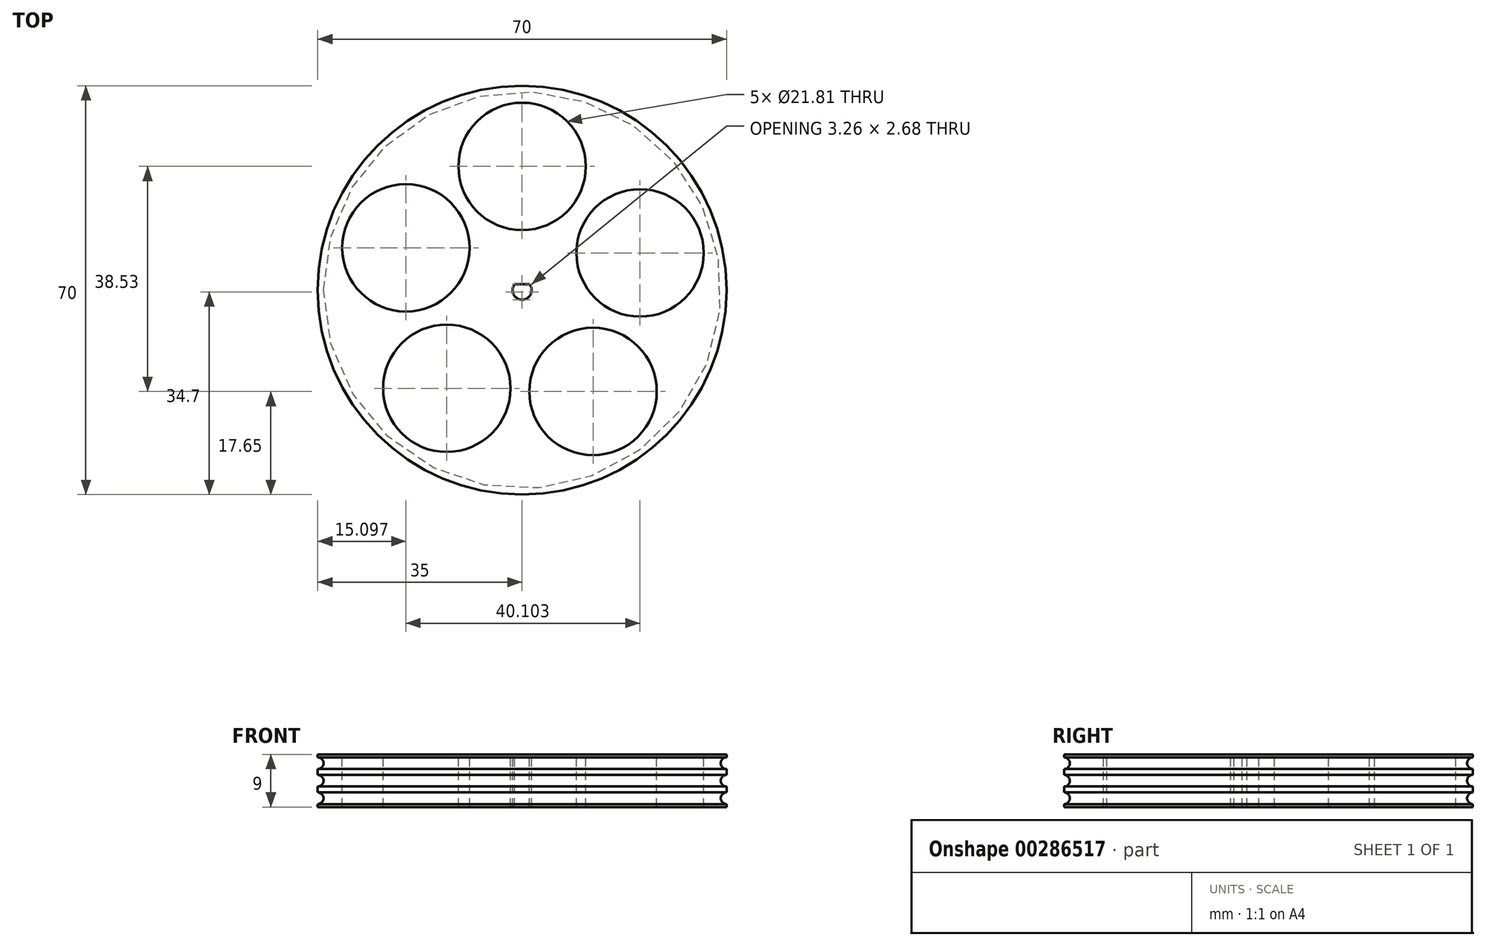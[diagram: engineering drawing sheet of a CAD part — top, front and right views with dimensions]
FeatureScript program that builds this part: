
annotation { "Feature Type Name" : "Feature", "Feature Type Description" : "" }
export const myFeature = defineFeature(function(context is Context, id is Id, definition is map)
    precondition{}
    {
        {
            var Q0;
            Q0=qCreatedBy(makeId("Front.planeOp"),FACE);
            var sketch = newSketch(context, id + "F0", { "sketchPlane" : qUnion([Q0])});
            skLineSegment(sketch, "E0.bottom", {"start": v(0, 0) * mm, "end": v(0, 9) * mm});
            skLineSegment(sketch, "E0.top", {"start": v(-35, 0) * mm, "end": v(-35, 9) * mm});
            skLineSegment(sketch, "E0.left", {"start": v(0, 0) * mm, "end": v(-35, 0) * mm});
            skLineSegment(sketch, "E0.right", {"start": v(0, 9) * mm, "end": v(-35, 9) * mm});
            skCircle(sketch, "E1", {"center": v(-35, 1.5) * mm, "radius": 1 * mm});
            skCircle(sketch, "E2.1.0.0", {"center": v(-35, 4.5) * mm, "radius": 1 * mm});
            skCircle(sketch, "E2.2.0.0", {"center": v(-35, 7.5) * mm, "radius": 1 * mm});
            skLineSegment(sketch, "E2.direction1", {"start": v(-35, 1.5) * mm, "end": v(-35, 4.5) * mm, "construction": true});
            skSolve(sketch);
        }
        {
            var Q0;
            Q0=makeQuery(id+"F0.imprint","IMPRINT",FACE,{"disambiguationData":[TD([[makeQuery(id+"F0.imprint","IMPRINT",EDGE,{"derivedFrom":sQuery(id+"F0.wireOp",EDGE,"E0.bottom")}),1.0]])]});
            var Q1;
            Q1=sQuery(id+"F0.wireOp",EDGE,"E0.bottom");
            revolve(context, id + "F1", {"surfaceOperationType" : NewSurfaceOperationType.NEW, "entities" : qUnion([Q0]), "axis" : qUnion([Q1]), "revolveType" : RevolveType.FULL});
        }
        {
            var Q0;
            Q0=makeQuery(id+"F1.opRevolve","SWEPT_FACE",FACE,{"disambiguationData":[OSD([sQuery(id+"F0.wireOp",EDGE,"E0.right")])]});
            var sketch = newSketch(context, id + "F2", { "sketchPlane" : qUnion([Q0])});
            skLineSegment(sketch, "E3", {"start": v(-1.2, 0.9) * mm, "end": v(1.2, 0.9) * mm, "construction": true});
            skArc(sketch, "E4", {"start": v(-1.2, 0.9) * mm, "mid": v(0, -1.5) * mm, "end": v(1.2, 0.9) * mm, "construction": true});
            skLineSegment(sketch, "E5.0", {"start": v(-1.27, 1.04) * mm, "end": v(1.27, 1.04) * mm});
            skArc(sketch, "E5.1", {"start": v(-1.27, 1.04) * mm, "mid": v(0, -1.64) * mm, "end": v(1.27, 1.04) * mm});
            skSolve(sketch);
        }
        {
            var Q0;
            Q0=qSketchRegion(id+"F2",true);
            extrude(context, id + "F3", {"entities" : qUnion([Q0]), "operationType" : NewBodyOperationType.REMOVE, "endBound" : BoundingType.THROUGH_ALL, "oppositeDirection" : true, "depth" : 25 * mm, "offsetDistance" : 25 * mm});
        }
        {
            var Q0;
            Q0=makeQuery(id+"F1.opRevolve","SWEPT_FACE",FACE,{"disambiguationData":[OSD([sQuery(id+"F0.wireOp",EDGE,"E0.right")])]});
            var sketch = newSketch(context, id + "F4", { "sketchPlane" : qUnion([Q0])});
            skCircle(sketch, "E6", {"center": v(0, 21.18) * mm, "radius": 10.9 * mm});
            skCircle(sketch, "E7.1.0", {"center": v(20.2, 6.37) * mm, "radius": 10.9 * mm});
            skCircle(sketch, "E7.2.0", {"center": v(12.15, -17.35) * mm, "radius": 10.9 * mm});
            skCircle(sketch, "E7.3.0", {"center": v(-12.9, -16.8) * mm, "radius": 10.9 * mm});
            skCircle(sketch, "E7.4.0", {"center": v(-19.9, 7.24) * mm, "radius": 10.9 * mm});
            skPoint(sketch, "E7.center", {"position": v(0, 0) * mm});
            skLineSegment(sketch, "E7.anchor1", {"start": v(0, 0) * mm, "end": v(0, 21.18) * mm, "construction": true});
            skLineSegment(sketch, "E7.anchor2", {"start": v(0, 0) * mm, "end": v(-19.9, 7.24) * mm, "construction": true});
            skSolve(sketch);
        }
        {
            var Q0;
            Q0=qSketchRegion(id+"F4",true);
            extrude(context, id + "F5", {"entities" : qUnion([Q0]), "operationType" : NewBodyOperationType.REMOVE, "endBound" : BoundingType.THROUGH_ALL, "oppositeDirection" : true, "depth" : 25 * mm, "offsetDistance" : 25 * mm});
        }
    });
